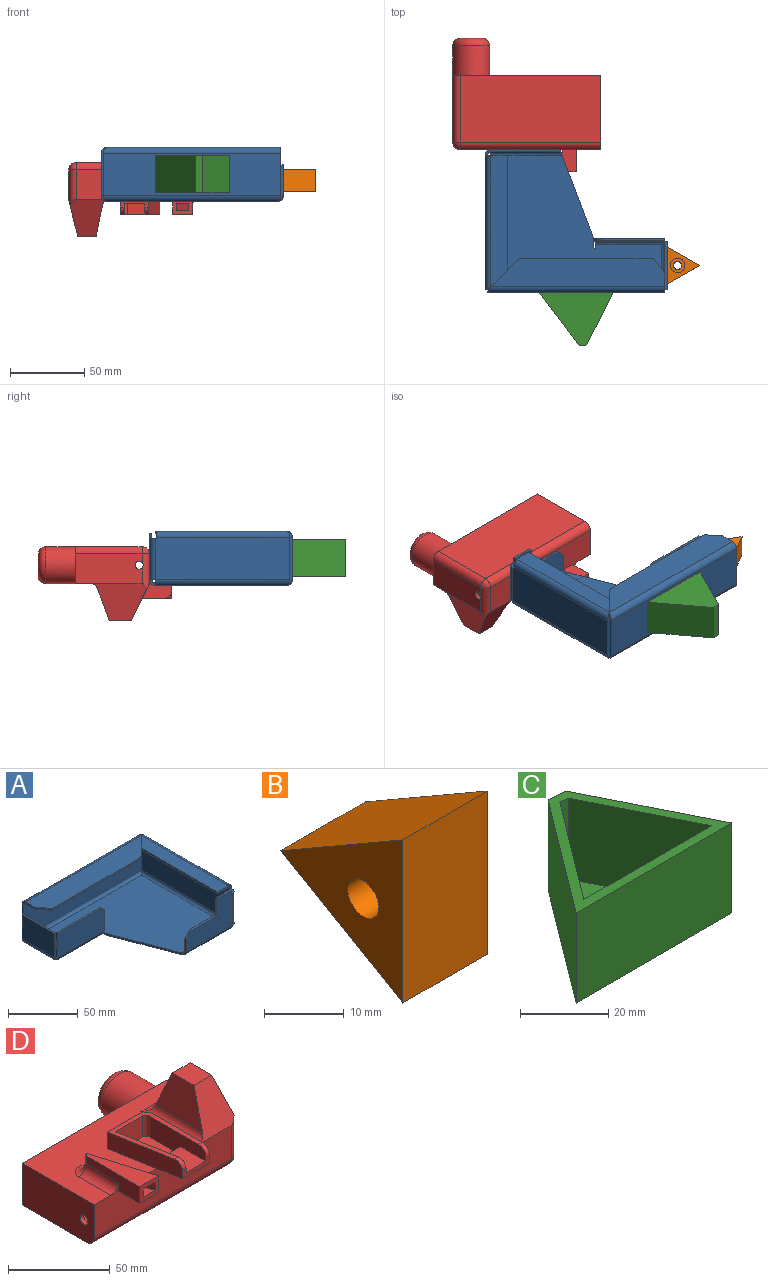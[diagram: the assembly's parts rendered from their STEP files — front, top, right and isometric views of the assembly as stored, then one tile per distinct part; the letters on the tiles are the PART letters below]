
ASSEMBLY  parts=4 mates=3
PART A: 94 faces, bbox 123x96.5x36.6 mm
  f0: plane 1.6x0.01mm, normal (0,-1,0), area 0mm2, adj f2,f3,f60,f82
  f1: plane 55.72x21.09mm, normal (-0.94,-0.35,0), area 95.3mm2, adj f2,f3,f8,f81
  f2: plane 115.16x88.66mm, normal (0,0,-1), area 6845.7mm2, adj f0,f1,f4,f5,f6,f7,f8,f9
  f3: plane 115.16x88.66mm, normal (0,0,1), area 6845.7mm2, adj f0,f1,f4,f5,f6,f7,f8,f9
  f4: plane 1.6x0.01mm, normal (-0.71,0.71,0), area 0mm2, adj f2,f3,f29,f90
  f5: plane 1.6x0.01mm, normal (0.71,0.71,0), area 0mm2, adj f2,f3,f28,f61
  f6: plane 1.68x1.6mm, normal (1,0,0), area 2.7mm2, adj f2,f3,f7,f72
  f7: cylinder r=0.85mm len=1.7mm, axis (0,0,1), area 4.3mm2, adj f2,f3,f6,f8
  f8: plane 6.17x1.6mm, normal (-1,0,0), area 9.9mm2, adj f1,f2,f3,f7
  f9: plane 1.6x0.01mm, normal (-0.71,-0.71,0), area 0mm2, adj f2,f3,f71,f91
  f10: plane 28.8x1.6mm, normal (1,0,0), area 46.1mm2, adj f14,f15,f25,f28
  f11: plane 21.1x1.6mm, normal (-1,0,0), area 33.8mm2, adj f12,f14,f15,f29
  f12: plane 7.7x1.6mm, normal (-1,0,0), area 12.3mm2, adj f11,f13,f14,f15
  f13: plane 1.6x0mm, normal (0,0,1), area 0mm2, adj f12,f14,f15,f24
  f14: plane 119.65x28.8mm, normal (0,1,0), area 3445.9mm2, adj f10,f11,f12,f13,f26,f30
  f15: plane 119.65x28.8mm, normal (0,-1,0), area 3445.9mm2, adj f10,f11,f12,f13,f27,f31
  f16: plane 88.29x1.6mm, normal (0,-1,0), area 141.3mm2, adj f20,f21,f22,f23
  f17: plane 6.54x6.54mm, normal (0.71,-0.71,0), area 14.8mm2, adj f18,f21,f22,f23
  f18: plane 11.09x11.09mm, normal (0.71,-0.71,0), area 25.1mm2, adj f17,f21,f22,f25
  f19: plane 9.2x1.6mm, normal (-1,0,0), area 14.7mm2, adj f20,f21,f22,f24
  f20: plane 9.9x7.9mm, normal (-0.78,-0.62,0), area 20.3mm2, adj f16,f19,f21,f22
  f21: plane 117.35x19.1mm, normal (0,0,1), area 2019.4mm2, adj f16,f17,f18,f19,f20,f23,f26
  f22: plane 117.35x19.1mm, normal (0,0,-1), area 2019.4mm2, adj f16,f17,f18,f19,f20,f23,f27
  f23: cylinder r=5mm len=3.54mm, axis (0,0,1), area 6.3mm2, adj f16,f17,f21,f22
  f24: plane 3.9x3.9mm, normal (-1,0,0), area 7.8mm2, adj f13,f19,f26,f27
  f25: bspline ~3.9x3.9mm, area 8.8mm2, adj f10,f18,f26,f27
  f26: cylinder r=3.9mm len=119.65mm, axis (-1,0,0), area 727.9mm2, adj f14,f21,f24,f25
  f27: cylinder r=2.3mm len=119.65mm, axis (-1,0,0), area 429.3mm2, adj f15,f22,f24,f25
  f28: bspline ~3.9x3.9mm, area 8.8mm2, adj f5,f10,f30,f31
  f29: bspline ~3.9x3.9mm, area 8.8mm2, adj f4,f11,f30,f31
  f30: cylinder r=3.9mm len=119.65mm, axis (1,0,0), area 722.8mm2, adj f2,f14,f28,f29
  f31: cylinder r=2.3mm len=119.65mm, axis (1,0,0), area 426.3mm2, adj f3,f15,f28,f29
  f32: plane 1.6x0.01mm, normal (0,-1,0), area 0mm2, adj f33,f34,f45,f60
  f33: plane 90.94x28.8mm, normal (1,0,0), area 2617.6mm2, adj f32,f35,f36,f37,f47,f58,f62
  f34: plane 90.94x28.8mm, normal (-1,0,0), area 2617.6mm2, adj f32,f35,f36,f37,f48,f59,f63
  f35: plane 28.8x1.6mm, normal (0,1,0), area 46.1mm2, adj f33,f34,f56,f61
  f36: plane 1.6x1.19mm, normal (0,0,1), area 1.9mm2, adj f33,f34,f37,f46
  f37: plane 1.6x1.19mm, normal (0,-1,0), area 1.9mm2, adj f33,f34,f36,f57
  f38: plane 14.91x1.6mm, normal (0,0,1), area 23.9mm2, adj f39,f40,f42,f44
  f39: plane 31.09x16.1mm, normal (0,-1,0), area 366.7mm2, adj f38,f41,f42,f43,f44,f47
  f40: plane 31.09x16.1mm, normal (0,1,0), area 366.7mm2, adj f38,f41,f42,f43,f44,f48
  f41: plane 16.1x16.1mm, normal (-0.71,0,-0.71), area 36.4mm2, adj f39,f40,f42,f45
  f42: plane 14.99x1.6mm, normal (-1,0,0), area 24mm2, adj f38,f39,f40,f41
  f43: plane 1.6x1.19mm, normal (0,0,1), area 1.9mm2, adj f39,f40,f44,f46
  f44: plane 3.49x1.6mm, normal (1,0,0), area 5.6mm2, adj f38,f39,f40,f43
  f45: plane 3.9x3.9mm, normal (0,0,-1), area 7.8mm2, adj f32,f41,f47,f48
  f46: plane 3.9x3.9mm, normal (0,0,1), area 7.8mm2, adj f36,f43,f47,f48
  f47: cylinder r=3.9mm len=27.6mm, axis (0,0,1), area 169.1mm2, adj f33,f39,f45,f46
  f48: cylinder r=2.3mm len=27.6mm, axis (0,0,1), area 99.7mm2, adj f34,f40,f45,f46
  f49: plane 9.91x1.6mm, normal (0,-1,0), area 15.9mm2, adj f50,f51,f53,f55
  f50: plane 88.64x11.1mm, normal (0,0,1), area 920.9mm2, adj f49,f52,f53,f54,f55,f58
  f51: plane 88.64x11.1mm, normal (0,0,-1), area 920.9mm2, adj f49,f52,f53,f54,f55,f59
  f52: plane 11.1x11.1mm, normal (-0.71,0.71,0), area 25.1mm2, adj f50,f51,f53,f56
  f53: plane 77.54x1.6mm, normal (-1,0,0), area 124.1mm2, adj f49,f50,f51,f52
  f54: plane 1.6x1.19mm, normal (0,-1,0), area 1.9mm2, adj f50,f51,f55,f57
  f55: plane 1.6x1.19mm, normal (1,0,0), area 1.9mm2, adj f49,f50,f51,f54
  f56: bspline ~3.9x3.9mm, area 8.8mm2, adj f35,f52,f58,f59
  f57: plane 3.9x3.9mm, normal (0,-1,0), area 7.8mm2, adj f37,f54,f58,f59
  f58: cylinder r=3.9mm len=89.75mm, axis (0,-1,0), area 544.7mm2, adj f33,f50,f56,f57
  f59: cylinder r=2.3mm len=89.75mm, axis (0,-1,0), area 321.3mm2, adj f34,f51,f56,f57
  f60: plane 3.9x3.9mm, normal (0,-1,0), area 7.8mm2, adj f0,f32,f62,f63
  f61: bspline ~3.9x3.9mm, area 8.8mm2, adj f5,f35,f62,f63
  f62: cylinder r=3.9mm len=90.94mm, axis (0,-1,0), area 552mm2, adj f2,f33,f60,f61
  f63: cylinder r=2.3mm len=90.94mm, axis (0,-1,0), area 325.5mm2, adj f3,f34,f60,f61
  f64: plane 21.1x1.6mm, normal (-1,0,0), area 33.8mm2, adj f67,f68,f69,f71
  f65: plane 1.6x1.17mm, normal (0,0,-1), area 1.9mm2, adj f66,f68,f69,f72
  f66: plane 16.1x1.6mm, normal (1,0,0), area 25.8mm2, adj f65,f68,f69,f70
  f67: plane 42.79x1.6mm, normal (0,0,1), area 68.5mm2, adj f64,f68,f69,f70
  f68: plane 47.79x21.1mm, normal (0,-1,0), area 1003.1mm2, adj f64,f65,f66,f67,f70,f73
  f69: plane 47.79x21.1mm, normal (0,1,0), area 1003.1mm2, adj f64,f65,f66,f67,f70,f74
  f70: cylinder r=5mm len=5mm, axis (0,-1,0), area 12.6mm2, adj f66,f67,f68,f69
  f71: bspline ~3.9x3.9mm, area 8.8mm2, adj f9,f64,f73,f74
  f72: plane 3.9x3.9mm, normal (1,0,0), area 7.8mm2, adj f6,f65,f73,f74
  f73: cylinder r=3.9mm len=46.62mm, axis (-1,0,0), area 280.5mm2, adj f2,f68,f71,f72
  f74: cylinder r=2.3mm len=46.62mm, axis (-1,0,0), area 165.4mm2, adj f3,f69,f71,f72
  f75: plane 11.1x1.6mm, normal (-1,0,0), area 17.8mm2, adj f78,f79,f80,f81
  f76: plane 16.1x16.1mm, normal (0.71,0,0.71), area 36.4mm2, adj f77,f78,f79,f82
  f77: plane 25.75x1.6mm, normal (0,0,1), area 41.2mm2, adj f76,f78,f79,f80
  f78: plane 46.85x16.1mm, normal (0,-1,0), area 612.1mm2, adj f75,f76,f77,f80,f83
  f79: plane 46.85x16.1mm, normal (0,1,0), area 612.1mm2, adj f75,f76,f77,f80,f84
  f80: plane 5x5mm, normal (-0.71,0,0.71), area 11.3mm2, adj f75,f77,f78,f79
  f81: bspline ~3.9x3.9mm, area 8.1mm2, adj f1,f75,f83,f84
  f82: plane 3.9x3.9mm, normal (1,0,0), area 7.8mm2, adj f0,f76,f83,f84
  f83: cylinder r=3.9mm len=48.02mm, axis (-1,0,0), area 289.4mm2, adj f2,f78,f81,f82
  f84: cylinder r=2.3mm len=48.02mm, axis (-1,0,0), area 170.7mm2, adj f3,f79,f81,f82
  f85: plane 21.1x1.6mm, normal (0,1,0), area 33.8mm2, adj f87,f88,f89,f90
  f86: plane 21.1x1.6mm, normal (0,-1,0), area 33.8mm2, adj f87,f88,f89,f91
  f87: plane 33.01x1.68mm, normal (0,0,1), area 52.8mm2, adj f85,f86,f88,f89
  f88: plane 33.01x21.1mm, normal (-1,0,0), area 696.5mm2, adj f85,f86,f87,f92
  f89: plane 33.01x21.1mm, normal (1,0,0), area 696.5mm2, adj f85,f86,f87,f93
  f90: bspline ~3.9x3.89mm, area 8.8mm2, adj f4,f85,f92,f93
  f91: bspline ~3.91x3.9mm, area 8.8mm2, adj f9,f86,f92,f93
  f92: cylinder r=3.9mm len=33.02mm, axis (0,1,0), area 192mm2, adj f2,f88,f90,f91
  f93: cylinder r=2.3mm len=33.01mm, axis (0,1,0), area 113.2mm2, adj f3,f89,f90,f91
PART B: 8 faces, bbox 15x21.7x25 mm
  f0: plane 21.65x15mm, normal (0,0.5,0.87), area 375mm2, adj f1,f2,f3,f4
  f1: plane 25x15mm, normal (0,-1,0), area 375mm2, adj f0,f2,f3,f4
  f2: plane 21.65x15mm, normal (0,0.5,-0.87), area 375mm2, adj f0,f1,f3,f4
  f3: plane 25x21.65mm, normal (-1,0,0), area 246.9mm2, adj f0,f1,f2,f5
  f4: plane 25x21.65mm, normal (1,0,0), area 196mm2, adj f0,f1,f2,f7
  f5: cylinder r=2.75mm len=10mm, axis (1,0,0), area 172.8mm2, adj f3,f6
  f6: plane 9.75x9.75mm, normal (1,0,0), area 50.9mm2, adj f5,f7
  f7: cylinder r=4.88mm len=9.75mm, axis (1,0,0), area 153.2mm2, adj f4,f6
PART C: 11 faces, bbox 50x36x25 mm
  f0: plane 50x36mm, normal (0,0,1), area 320.4mm2, adj f1,f2,f3,f5,f6,f7,f8,f10
  f1: plane 35.53x25mm, normal (0.89,0.45,0), area 993mm2, adj f0,f3,f4,f5
  f2: plane 36x27mm, normal (-0.8,0.6,0), area 1125mm2, adj f0,f3,f4,f5
  f3: plane 50x25mm, normal (0,-1,0), area 1250mm2, adj f0,f1,f2,f4
  f4: plane 50x36mm, normal (0,0,-1), area 988.8mm2, adj f1,f2,f3,f5
  f5: plane 25x5.24mm, normal (0.09,1,0), area 131.4mm2, adj f0,f1,f2,f4
  f6: plane 30.66x22.5mm, normal (-0.89,-0.45,0), area 771.4mm2, adj f0,f8,f9,f10
  f7: plane 30.89x23.16mm, normal (0.8,-0.6,0), area 868.6mm2, adj f0,f8,f9,f10
  f8: plane 40.96x22.5mm, normal (0,1,0), area 921.5mm2, adj f0,f6,f7,f9
  f9: plane 40.96x30.89mm, normal (0,0,1), area 668.5mm2, adj f6,f7,f8,f10
  f10: plane 22.5x2.46mm, normal (-0.09,-1,0), area 55.6mm2, adj f0,f6,f7,f9
PART D: 63 faces, bbox 101x90x51 mm
  f0: plane 44.09x10mm, normal (-0.98,-0.17,0), area 442.3mm2, adj f2,f3,f21,f25,f47,f49
  f1: plane 39.09x10mm, normal (1,0,0), area 385.5mm2, adj f2,f3,f21,f26,f47,f48
  f2: plane 39.09x26.66mm, normal (0,0,1), area 246.4mm2, adj f0,f1,f8,f9,f25,f26,f40,f41
  f3: plane 21.51x15mm, normal (0,0,-1), area 302.7mm2, adj f0,f1,f20,f47
  f4: plane 37.55x11.26mm, normal (0.96,0.29,0), area 274.3mm2, adj f6,f7,f20,f27,f46,f59
  f5: plane 37.27x10mm, normal (-1,0,0), area 261.3mm2, adj f6,f7,f20,f27,f46,f57
  f6: plane 38.27x13.21mm, normal (0,0,1), area 285.9mm2, adj f4,f5,f27,f46
  f7: plane 15x13.21mm, normal (0,0,-1), area 164.5mm2, adj f4,f5,f20,f46
  f8: plane 41.59x12.5mm, normal (0.98,0.17,0), area 433.6mm2, adj f2,f10,f35,f36,f40,f47,f49
  f9: plane 39.09x12.5mm, normal (-1,0,0), area 395.7mm2, adj f2,f10,f35,f36,f41,f47,f48
  f10: plane 17.5x16.91mm, normal (0,0,1), area 268.9mm2, adj f8,f9,f35,f47
  f11: plane 27.04x10mm, normal (-0.96,-0.29,0), area 190.9mm2, adj f12,f13,f14,f35,f36,f46
  f12: plane 27.04x10mm, normal (1,0,0), area 182.9mm2, adj f11,f13,f14,f35,f36,f46
  f13: plane 27.04x8.1mm, normal (0,0,-1), area 109.6mm2, adj f11,f12,f46
  f14: plane 17.5x8.1mm, normal (0,0,1), area 95.9mm2, adj f11,f12,f35,f46
  f15: plane 12.5x12.5mm, normal (0,1,0), area 33.5mm2, adj f17,f21,f23
  f16: plane 12.5x12.5mm, normal (0,1,0), area 28.2mm2, adj f17,f22,f23,f29
  f17: plane 45x20mm, normal (1,0,0), area 878.2mm2, adj f15,f16,f21,f29,f45,f51,f62
  f18: plane 87.5x25mm, normal (0,1,0), area 1942.1mm2, adj f19,f21,f22,f23
  f19: plane 50x25mm, normal (-1,0,0), area 1220.9mm2, adj f18,f20,f21,f22,f44,f60
  f20: plane 95x25mm, normal (0,-1,0), area 1911mm2, adj f3,f4,f5,f7,f19,f21,f54,f57
  f21: plane 100x50mm, normal (0,0,1), area 2798.5mm2, adj f0,f1,f15,f17,f18,f19,f20,f25
  f22: plane 95x45mm, normal (0,0,-1), area 4275mm2, adj f16,f18,f19,f29,f60
  f23: cylinder r=12.5mm len=25mm, axis (0,-1,0), area 1570.8mm2, adj f15,f16,f18,f28
  f24: plane 15x15mm, normal (0,1,0), area 176.7mm2, adj f28
  f25: plane 21.66x10mm, normal (0,1,0), area 216.6mm2, adj f0,f2,f21,f26
  f26: cylinder r=5mm len=10mm, axis (0,0,-1), area 78.5mm2, adj f1,f2,f21,f25
  f27: cylinder r=1mm len=5mm, axis (0,0,-1), area 14.3mm2, adj f4,f5,f6,f58
  f28: torus R=7.5mm, axis (0,1,0), area 527.2mm2, adj f23,f24
  f29: cylinder r=5mm len=45mm, axis (0,1,0), area 353.4mm2, adj f16,f17,f22,f61
  f30: plane 10x10mm, normal (0,-1,0), area 21.5mm2, adj f32,f36,f38
  f31: plane 10x10mm, normal (0,-1,0), area 20.1mm2, adj f32,f37,f38,f43
  f32: plane 45x17.5mm, normal (-1,0,0), area 763.7mm2, adj f30,f31,f35,f36,f43,f45
  f33: plane 85x20mm, normal (0,-1,0), area 1542.9mm2, adj f34,f36,f37,f38
  f34: plane 45x20mm, normal (1,0,0), area 876.2mm2, adj f33,f35,f36,f37,f44
  f35: plane 95x25mm, normal (0,1,0), area 1997.5mm2, adj f8,f9,f10,f11,f12,f14,f32,f34
  f36: plane 95x45mm, normal (0,0,-1), area 3804mm2, adj f8,f9,f11,f12,f30,f32,f33,f34
  f37: plane 92.5x45mm, normal (0,0,1), area 4162.5mm2, adj f31,f33,f34,f35,f43
  f38: cylinder r=10mm len=22.5mm, axis (0,-1,0), area 1413.7mm2, adj f30,f31,f33,f42
  f39: plane 15x15mm, normal (0,-1,0), area 176.7mm2, adj f42
  f40: plane 18.68x12.5mm, normal (0,-1,0), area 233.4mm2, adj f2,f8,f36,f41
  f41: cylinder r=2.5mm len=12.5mm, axis (0,0,-1), area 49.1mm2, adj f2,f9,f36,f40
  f42: torus R=7.5mm, axis (0,1,0), area 224.3mm2, adj f38,f39
  f43: cylinder r=2.5mm len=45mm, axis (0,1,0), area 176.7mm2, adj f31,f32,f35,f37
  f44: cylinder r=2.75mm len=5.5mm, axis (1,0,0), area 43.2mm2, adj f19,f34
  f45: cylinder r=2.75mm len=5.5mm, axis (1,0,0), area 43.1mm2, adj f17,f32,f62
  f46: plane 13.21x10mm, normal (0,-1,0), area 91.6mm2, adj f4,f5,f6,f7,f11,f12,f13,f14
  f47: plane 18.85x5mm, normal (0,-1,0), area 59.7mm2, adj f0,f1,f3,f8,f9,f10,f48,f49
  f48: cylinder r=5mm len=5mm, axis (1,0,0), area 19.6mm2, adj f1,f2,f9,f47
  f49: cylinder r=5mm len=5mm, axis (1,0,0), area 19.9mm2, adj f0,f2,f8,f47
  f50: plane 14.92x12.3mm, normal (0,0,1), area 183.4mm2, adj f51,f52,f53,f54
  f51: plane 37.8x25mm, normal (0.97,0,0.24), area 653.4mm2, adj f17,f50,f52,f54,f55,f62
  f52: plane 22.21x21.73mm, normal (0,0.94,0.34), area 398.6mm2, adj f50,f51,f53,f55,f56
  f53: plane 32.89x21.01mm, normal (-0.98,0,0.2), area 513mm2, adj f50,f52,f54,f56
  f54: plane 26.7x25mm, normal (0,-0.9,0.44), area 495.6mm2, adj f20,f50,f51,f53,f56,f62
  f55: cylinder r=5mm len=27.7mm, axis (1,0,0), area 150.7mm2, adj f21,f51,f52,f56
  f56: cylinder r=5mm len=39.79mm, axis (0,-1,0), area 247.2mm2, adj f21,f52,f53,f54,f55
  f57: cylinder r=5mm len=22.27mm, axis (0,-1,0), area 174.9mm2, adj f5,f20,f21,f58
  f58: torus R=6mm, axis (0,0,1), area 63.1mm2, adj f21,f27,f57,f59
  f59: cylinder r=5mm len=25.43mm, axis (-0.29,0.96,0), area 189.2mm2, adj f4,f20,f21,f58
  f60: cylinder r=5mm len=95mm, axis (1,0,0), area 746.1mm2, adj f19,f20,f22,f61
  f61: sphere r=5mm, area 39.3mm2, adj f29,f60,f62
  f62: cylinder r=5mm len=24.08mm, axis (0,0,-1), area 166.1mm2, adj f17,f20,f45,f51,f54,f61
PLACE A rot(axis=(0,0,1),180deg) t=(-63.6,31.25,-24.29)mm fixed
PLACE B rot(axis=(-0.58,-0.58,-0.58),120.1deg) t=(27.83,-26.36,-67.34)mm
PLACE C rot(axis=(-1,0,0),180deg) t=(-33.63,-6.92,6.51)mm
PLACE D rot(axis=(0,1,0),180deg) t=(-92,89.53,2.02)mm
MATE fastened C.f3 <-> A.f14  axis (0,1,0) through (-58.63,-31.92,-5.99)mm
MATE fastened B.f1 <-> A.f88  axis (-1,0,0) through (2.86,-13.8,-9.84)mm
MATE fastened A.f78 <-> D.f20  axis (0,1,0) through (-89.35,64.53,-13.04)mm
